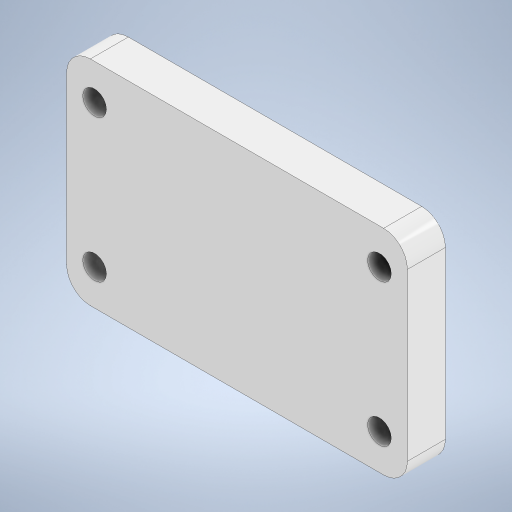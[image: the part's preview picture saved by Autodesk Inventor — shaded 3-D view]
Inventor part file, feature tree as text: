
AUTODESK INVENTOR PART (.ipt)
format: ipt  version: 2023 (Build 270158000, 158)  size: 263,680 bytes
history: native  units: mm
features: extrude x4, sketch x4, chamfer x1
ambient origin geometry x8: Origin, YZ Plane, XZ Plane, XY Plane, X Axis, Y Axis, Z Axis, Center Point
bodies: Solid1 (feature_tree)
feature tree (9):
  extrude  "Extrusion1"  Depth=16.0mm
  extrude  "Extrusion2"  Depth=13.25mm TaperAngle=0.0deg
  extrude  "Extrusion3"  Depth=22.0mm
  extrude  "Extrusion4"  Depth=49.75mm TaperAngle=0.0deg
  sketch  "Sketch1"  dims[d0=5.75mm d1=0.0mm d2=16.0mm]
  sketch  "Sketch2"  dims[d3=16.0mm d4=13.25mm d5=0.0mm]
  sketch  "Sketch3"  dims[d6=49.75mm d7=0.0mm d8=22.0mm]
  sketch  "Sketch4"  dims[d9=52.0mm d10=49.75mm d11=0.0mm]
  chamfer  "Chamfer3"  [1 undecoded]
note: 1 required parameter value undecoded (feature->parameter linkage not recoverable at this tier; creation-order binding heuristic only, values carry confidence <= 0.55)
